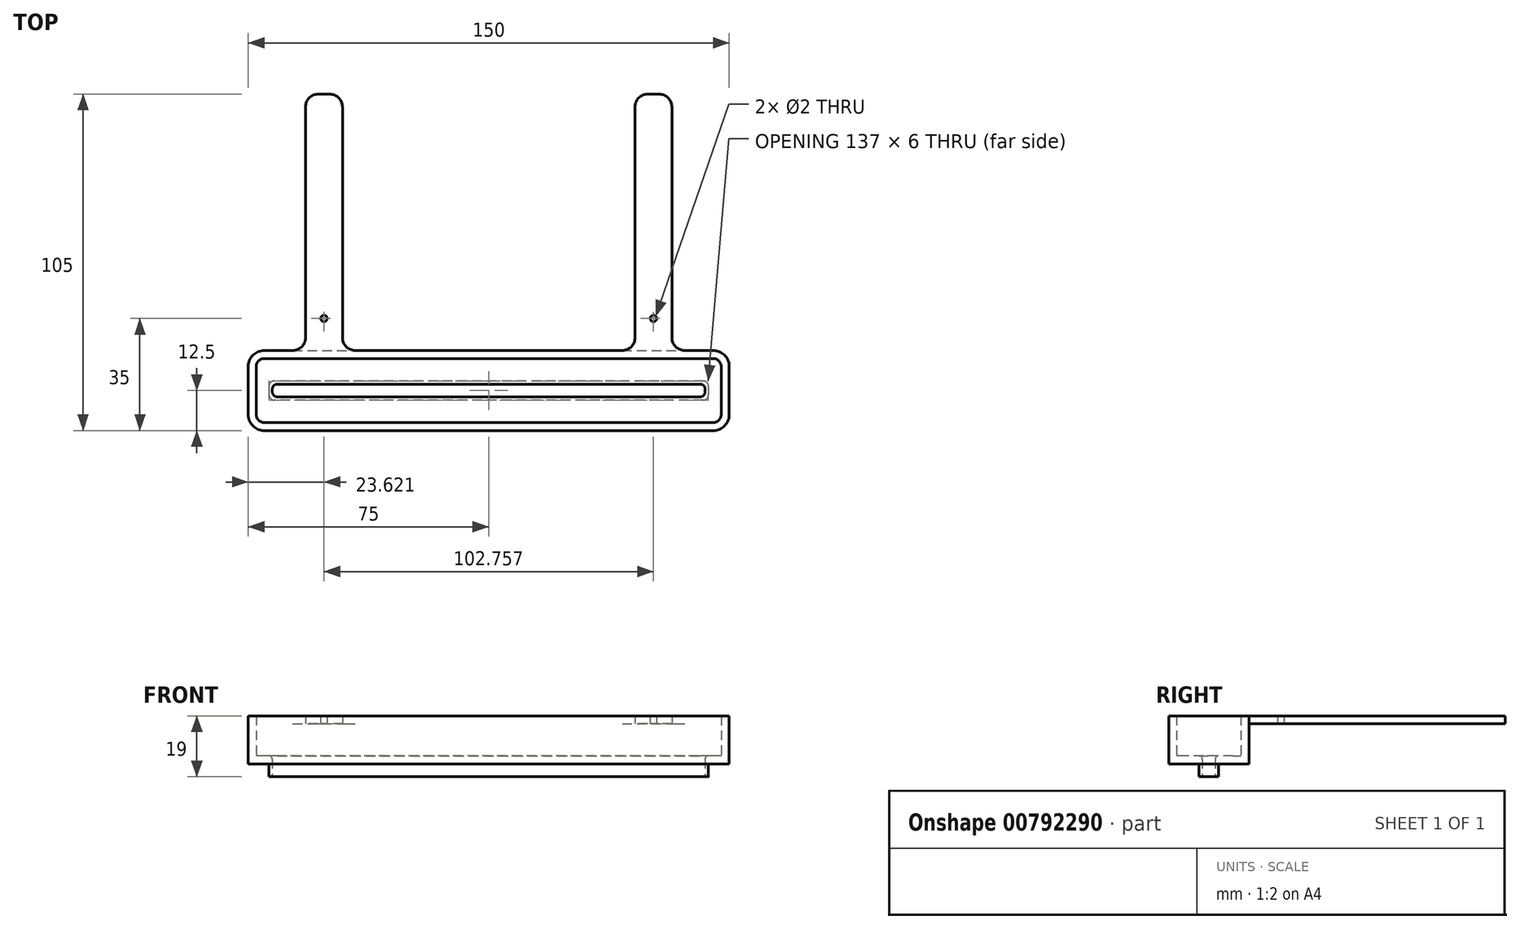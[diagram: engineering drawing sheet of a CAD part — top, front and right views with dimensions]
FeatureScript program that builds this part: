
annotation { "Feature Type Name" : "Feature", "Feature Type Description" : "" }
export const myFeature = defineFeature(function(context is Context, id is Id, definition is map)
    precondition{}
    {
        {
            var Q0;
            Q0=qCreatedBy(makeId("Top.planeOp"),FACE);
            var sketch = newSketch(context, id + "F0", { "sketchPlane" : qUnion([Q0])});
            skLineSegment(sketch, "E0.bottom", {"start": v(70, 12.5) * mm, "end": v(61.13, 12.5) * mm});
            skLineSegment(sketch, "E0.top", {"start": v(70, -12.5) * mm, "end": v(-70, -12.5) * mm});
            skLineSegment(sketch, "E0.left", {"start": v(75, 7.5) * mm, "end": v(75, -7.5) * mm});
            skLineSegment(sketch, "E0.right", {"start": v(-75, 7.5) * mm, "end": v(-75, -7.5) * mm});
            skPoint(sketch, "E0.middle", {"position": v(0, 0) * mm});
            skPoint(sketch, "E1.visualSharp", {"position": v(-75, 12.5) * mm});
            skArc(sketch, "E1.filletArc", {"start": v(-70, 12.5) * mm, "mid": v(-73.54, 11.04) * mm, "end": v(-75, 7.5) * mm});
            skPoint(sketch, "E2.visualSharp", {"position": v(-75, -12.5) * mm});
            skArc(sketch, "E2.filletArc", {"start": v(-75, -7.5) * mm, "mid": v(-73.54, -11.04) * mm, "end": v(-70, -12.5) * mm});
            skPoint(sketch, "E3.visualSharp", {"position": v(75, 12.5) * mm});
            skArc(sketch, "E3.filletArc", {"start": v(75, 7.5) * mm, "mid": v(73.54, 11.04) * mm, "end": v(70, 12.5) * mm});
            skPoint(sketch, "E4.visualSharp", {"position": v(75, -12.5) * mm});
            skArc(sketch, "E4.filletArc", {"start": v(70, -12.5) * mm, "mid": v(73.54, -11.04) * mm, "end": v(75, -7.5) * mm});
            skLineSegment(sketch, "E5.bottom", {"start": v(65.9, -2) * mm, "end": v(-65.9, -2) * mm});
            skLineSegment(sketch, "E5.top", {"start": v(65.9, 2) * mm, "end": v(-65.9, 2) * mm});
            skLineSegment(sketch, "E5.left", {"start": v(67.5, -0.4) * mm, "end": v(67.5, 0.4) * mm});
            skLineSegment(sketch, "E5.right", {"start": v(-67.5, -0.4) * mm, "end": v(-67.5, 0.4) * mm});
            skPoint(sketch, "E6.visualSharp", {"position": v(-67.5, 2) * mm});
            skArc(sketch, "E6.filletArc", {"start": v(-65.9, 2) * mm, "mid": v(-67.03, 1.53) * mm, "end": v(-67.5, 0.4) * mm});
            skPoint(sketch, "E7.visualSharp", {"position": v(-67.5, -2) * mm});
            skArc(sketch, "E7.filletArc", {"start": v(-67.5, -0.4) * mm, "mid": v(-67.03, -1.53) * mm, "end": v(-65.9, -2) * mm});
            skPoint(sketch, "E8.visualSharp", {"position": v(67.5, 2) * mm});
            skArc(sketch, "E8.filletArc", {"start": v(67.5, 0.4) * mm, "mid": v(67.03, 1.53) * mm, "end": v(65.9, 2) * mm});
            skPoint(sketch, "E9.visualSharp", {"position": v(67.5, -2) * mm});
            skArc(sketch, "E9.filletArc", {"start": v(65.9, -2) * mm, "mid": v(67.03, -1.53) * mm, "end": v(67.5, -0.4) * mm});
            skLineSegment(sketch, "E10.bottom", {"start": v(66.9, 3) * mm, "end": v(-66.9, 3) * mm});
            skLineSegment(sketch, "E10.top", {"start": v(66.9, -3) * mm, "end": v(-66.9, -3) * mm});
            skLineSegment(sketch, "E10.left", {"start": v(68.5, 1.4) * mm, "end": v(68.5, -1.4) * mm});
            skLineSegment(sketch, "E10.right", {"start": v(-68.5, 1.4) * mm, "end": v(-68.5, -1.4) * mm});
            skPoint(sketch, "E11.visualSharp", {"position": v(-68.5, 3) * mm});
            skArc(sketch, "E11.filletArc", {"start": v(-66.9, 3) * mm, "mid": v(-68.03, 2.53) * mm, "end": v(-68.5, 1.4) * mm});
            skPoint(sketch, "E12.visualSharp", {"position": v(-68.5, -3) * mm});
            skArc(sketch, "E12.filletArc", {"start": v(-68.5, -1.4) * mm, "mid": v(-68.03, -2.53) * mm, "end": v(-66.9, -3) * mm});
            skPoint(sketch, "E13.visualSharp", {"position": v(68.5, 3) * mm});
            skArc(sketch, "E13.filletArc", {"start": v(68.5, 1.4) * mm, "mid": v(68.03, 2.53) * mm, "end": v(66.9, 3) * mm});
            skPoint(sketch, "E14.visualSharp", {"position": v(68.5, -3) * mm});
            skArc(sketch, "E14.filletArc", {"start": v(66.9, -3) * mm, "mid": v(68.03, -2.53) * mm, "end": v(68.5, -1.4) * mm});
            skLineSegment(sketch, "E15.top", {"start": v(-53.13, 92.5) * mm, "end": v(-49.63, 92.5) * mm});
            skLineSegment(sketch, "E15.left", {"start": v(-57.13, 16.5) * mm, "end": v(-57.13, 88.5) * mm});
            skLineSegment(sketch, "E15.right", {"start": v(-45.63, 16.5) * mm, "end": v(-45.63, 88.5) * mm});
            skLineSegment(sketch, "E16.MirrorCS", {"start": v(45.63, 16.5) * mm, "end": v(45.63, 88.5) * mm});
            skLineSegment(sketch, "E17.MirrorCS", {"start": v(57.13, 16.5) * mm, "end": v(57.13, 88.5) * mm});
            skLineSegment(sketch, "E18.MirrorCS", {"start": v(53.13, 92.5) * mm, "end": v(49.63, 92.5) * mm});
            skLineSegment(sketch, "E19.trimOffspring", {"start": v(-61.13, 12.5) * mm, "end": v(-70, 12.5) * mm});
            skLineSegment(sketch, "E20.trimOffspring", {"start": v(41.63, 12.5) * mm, "end": v(-41.63, 12.5) * mm});
            skPoint(sketch, "E21.visualSharp", {"position": v(-57.13, 12.5) * mm});
            skArc(sketch, "E21.filletArc", {"start": v(-61.13, 12.5) * mm, "mid": v(-58.3, 13.67) * mm, "end": v(-57.13, 16.5) * mm});
            skPoint(sketch, "E22.visualSharp", {"position": v(-45.63, 12.5) * mm});
            skArc(sketch, "E22.filletArc", {"start": v(-45.63, 16.5) * mm, "mid": v(-44.46, 13.67) * mm, "end": v(-41.63, 12.5) * mm});
            skPoint(sketch, "E23.visualSharp", {"position": v(45.63, 12.5) * mm});
            skArc(sketch, "E23.filletArc", {"start": v(41.63, 12.5) * mm, "mid": v(44.46, 13.67) * mm, "end": v(45.63, 16.5) * mm});
            skPoint(sketch, "E24.visualSharp", {"position": v(57.13, 12.5) * mm});
            skArc(sketch, "E24.filletArc", {"start": v(57.13, 16.5) * mm, "mid": v(58.3, 13.67) * mm, "end": v(61.13, 12.5) * mm});
            skPoint(sketch, "E25.visualSharp", {"position": v(-57.13, 92.5) * mm});
            skArc(sketch, "E25.filletArc", {"start": v(-53.13, 92.5) * mm, "mid": v(-55.96, 91.33) * mm, "end": v(-57.13, 88.5) * mm});
            skPoint(sketch, "E26.visualSharp", {"position": v(-45.63, 92.5) * mm});
            skArc(sketch, "E26.filletArc", {"start": v(-45.63, 88.5) * mm, "mid": v(-46.8, 91.33) * mm, "end": v(-49.63, 92.5) * mm});
            skPoint(sketch, "E27.visualSharp", {"position": v(45.63, 92.5) * mm});
            skArc(sketch, "E27.filletArc", {"start": v(49.63, 92.5) * mm, "mid": v(46.8, 91.33) * mm, "end": v(45.63, 88.5) * mm});
            skPoint(sketch, "E28.visualSharp", {"position": v(57.13, 92.5) * mm});
            skArc(sketch, "E28.filletArc", {"start": v(57.13, 88.5) * mm, "mid": v(55.96, 91.33) * mm, "end": v(53.13, 92.5) * mm});
            skLineSegment(sketch, "E29", {"start": v(-61.13, 12.5) * mm, "end": v(-41.63, 12.5) * mm});
            skLineSegment(sketch, "E30", {"start": v(41.63, 12.5) * mm, "end": v(61.13, 12.5) * mm});
            skCircle(sketch, "E31", {"center": v(-51.38, 22.5) * mm, "radius": 1 * mm});
            skPoint(sketch, "E31.centerSnap0", {"position": v(-51.38, 12.5) * mm});
            skCircle(sketch, "E32", {"center": v(51.38, 22.5) * mm, "radius": 1 * mm});
            skPoint(sketch, "E32.centerSnap0", {"position": v(51.38, 12.5) * mm});
            skSolve(sketch);
        }
        {
            var Q0;
            Q0=makeQuery(id+"F0.imprint","IMPRINT",FACE,{"disambiguationData":[TD([[makeQuery(id+"F0.imprint","IMPRINT",EDGE,{"derivedFrom":sQuery(id+"F0.wireOp",EDGE,"E0.bottom")}),1.0]])]});
            var Q1;
            Q1=makeQuery(id+"F0.imprint","IMPRINT",FACE,{"disambiguationData":[TD([[makeQuery(id+"F0.imprint","IMPRINT",EDGE,{"derivedFrom":sQuery(id+"F0.wireOp",EDGE,"E5.bottom")}),1.0]])]});
            var Q2;
            Q2=makeQuery(id+"F0.imprint","IMPRINT",FACE,{"disambiguationData":[TD([[makeQuery(id+"F0.imprint","IMPRINT",EDGE,{"derivedFrom":sQuery(id+"F0.wireOp",EDGE,"E5.bottom")}),-1.0]])]});
            extrude(context, id + "F1", {"entities" : qUnion([Q0, Q1, Q2]), "depth" : 15 * mm, "offsetDistance" : 25 * mm});
        }
        {
            var Q0;
            Q0=makeQuery(id+"F1.opExtrude","CAP_FACE",FACE,{"disambiguationData":[OSD([sQuery(id+"F0.wireOp",EDGE,"E0.bottom"),sQuery(id+"F0.wireOp",EDGE,"E0.top"),sQuery(id+"F0.wireOp",EDGE,"E0.left"),sQuery(id+"F0.wireOp",EDGE,"E0.right"),sQuery(id+"F0.wireOp",EDGE,"E1.filletArc"),sQuery(id+"F0.wireOp",EDGE,"E2.filletArc"),sQuery(id+"F0.wireOp",EDGE,"E3.filletArc"),sQuery(id+"F0.wireOp",EDGE,"E4.filletArc"),sQuery(id+"F0.wireOp",EDGE,"E19.trimOffspring"),sQuery(id+"F0.wireOp",EDGE,"E20.trimOffspring"),sQuery(id+"F0.wireOp",EDGE,"E29"),sQuery(id+"F0.wireOp",EDGE,"E30")])],"isStart":false});
            shell(context, id + "F2", {"entities" : qUnion([Q0]), "thickness" : 2.5 * mm});
        }
        {
            var Q0;
            Q0=makeQuery(id+"F0.imprint","IMPRINT",FACE,{"disambiguationData":[TD([[makeQuery(id+"F0.imprint","IMPRINT",EDGE,{"derivedFrom":sQuery(id+"F0.wireOp",EDGE,"E5.bottom")}),-1.0]])]});
            extrude(context, id + "F3", {"entities" : qUnion([Q0]), "operationType" : NewBodyOperationType.REMOVE, "depth" : 3 * mm, "offsetDistance" : 25 * mm});
        }
        {
            var Q0;
            Q0=makeQuery(id+"F0.imprint","IMPRINT",FACE,{"disambiguationData":[TD([[makeQuery(id+"F0.imprint","IMPRINT",EDGE,{"derivedFrom":sQuery(id+"F0.wireOp",EDGE,"E5.bottom")}),1.0]])]});
            extrude(context, id + "F4", {"entities" : qUnion([Q0]), "operationType" : NewBodyOperationType.ADD, "oppositeDirection" : true, "depth" : 4 * mm, "offsetDistance" : 25 * mm});
        }
        {
            var Q0;
            Q0=makeQuery(id+"F4.opExtrude","CAP_EDGE",EDGE,{"disambiguationData":[OSD([sQuery(id+"F0.wireOp",EDGE,"E5.bottom")])],"isStart":false});
            var Q1;
            Q1=makeQuery(id+"F4.opExtrude","CAP_EDGE",EDGE,{"disambiguationData":[OSD([sQuery(id+"F0.wireOp",EDGE,"E7.filletArc")])],"isStart":false});
            fillet(context, id + "F5", {"entities" : qUnion([Q0, Q1]), "radius" : 0.5 * mm, "tangentPropagation" : true, "allowEdgeOverflow" : false});
        }
        {
            var Q0;
            Q0=makeQuery(id+"F3.boolean.opBoolean","INTERSECT",EDGE,{"derivedFrom":[makeQuery(id+"F2.opShell","OFFSET_FACE",FACE,{"disambiguationData":[OSD([sQuery(id+"F0.wireOp",EDGE,"E0.bottom"),sQuery(id+"F0.wireOp",EDGE,"E0.top"),sQuery(id+"F0.wireOp",EDGE,"E0.left"),sQuery(id+"F0.wireOp",EDGE,"E0.right"),sQuery(id+"F0.wireOp",EDGE,"E1.filletArc"),sQuery(id+"F0.wireOp",EDGE,"E2.filletArc"),sQuery(id+"F0.wireOp",EDGE,"E3.filletArc"),sQuery(id+"F0.wireOp",EDGE,"E4.filletArc"),sQuery(id+"F0.wireOp",EDGE,"E19.trimOffspring"),sQuery(id+"F0.wireOp",EDGE,"E20.trimOffspring"),sQuery(id+"F0.wireOp",EDGE,"E29"),sQuery(id+"F0.wireOp",EDGE,"E30")])]}),makeQuery(id+"F3.opExtrude","SWEPT_FACE",FACE,{"disambiguationData":[OSD([sQuery(id+"F0.wireOp",EDGE,"E5.top")])]})]});
            fillet(context, id + "F6", {"entities" : qUnion([Q0]), "radius" : 1 * mm, "tangentPropagation" : true, "allowEdgeOverflow" : false});
        }
        {
            var Q0;
            Q0=makeQuery(id+"F0.imprint","IMPRINT",FACE,{"disambiguationData":[TD([[makeQuery(id+"F0.imprint","IMPRINT",EDGE,{"derivedFrom":sQuery(id+"F0.wireOp",EDGE,"E16.MirrorCS")}),-1.0]])]});
            var Q1;
            Q1=makeQuery(id+"F0.imprint","IMPRINT",FACE,{"disambiguationData":[TD([[makeQuery(id+"F0.imprint","IMPRINT",EDGE,{"derivedFrom":sQuery(id+"F0.wireOp",EDGE,"E15.top")}),-1.0]])]});
            extrude(context, id + "F7", {"entities" : qUnion([Q0, Q1]), "operationType" : NewBodyOperationType.ADD, "depth" : 15 * mm, "offsetDistance" : 25 * mm, "hasSecondDirection" : true, "secondDirectionOppositeDirection" : false, "secondDirectionDepth" : 12.5 * mm});
        }
    });
